FCSTD DOCUMENT  (FreeCAD 0.19R24276 (Git))
Label: Bearing_fix_22x8x7_P2
License: All rights reserved
LicenseURL: http://en.wikipedia.org/wiki/All_rights_reserved
objects: Sketcher::SketchObject×1, PartDesign::Body×1
note: 2 computed .brp shape members not serialized (recipe doc carries the construction recipe); baked Part::Feature solids carry a one-line shape summary decoded from their .brp

FEATURE [Sketcher::SketchObject] Sketch
  FullyConstrained = true
  MapMode = 5
  Support = -> [XY_Plane]
  sketch-geometry (30):
    g0: Circle CenterX=8.3 CenterY=-44.5 CenterZ=0 NormalX=0 NormalY=0 NormalZ=1 AngleXU=0 Radius=2.5
    g1: Circle CenterX=26.7 CenterY=-44.5 CenterZ=0 NormalX=0 NormalY=0 NormalZ=1 AngleXU=0 Radius=2.5
    g2: Circle CenterX=8.3 CenterY=-23.5 CenterZ=0 NormalX=0 NormalY=0 NormalZ=1 AngleXU=0 Radius=2.5
    g3: Circle CenterX=26.7 CenterY=-23.5 CenterZ=0 NormalX=0 NormalY=0 NormalZ=1 AngleXU=0 Radius=2.5
    g4: LineSegment StartX=0 StartY=-50 StartZ=0 EndX=35 EndY=-50 EndZ=0
    g5: LineSegment StartX=35 StartY=-50 StartZ=0 EndX=35 EndY=0 EndZ=0
    g6: LineSegment StartX=35 StartY=0 StartZ=0 EndX=0 EndY=0 EndZ=0
    g7: LineSegment StartX=0 StartY=0 StartZ=0 EndX=0 EndY=-50 EndZ=0
    g8: LineSegment StartX=8.3 StartY=-44.5 StartZ=0 EndX=26.7 EndY=-23.5 EndZ=0
    g9: LineSegment StartX=8.3 StartY=-23.5 StartZ=0 EndX=26.7 EndY=-44.5 EndZ=0
    g10: GeomPoint X=17.5 Y=-34 Z=0
    g11: GeomPoint X=17.5 Y=-34 Z=0
    g12: Circle CenterX=17.5 CenterY=-34 CenterZ=0 NormalX=0 NormalY=0 NormalZ=1 AngleXU=0 Radius=5.5
    g13: LineSegment StartX=17.5 StartY=-34 StartZ=0 EndX=17.5 EndY=-50 EndZ=0
    g14: Circle CenterX=17.5 CenterY=-34 CenterZ=0 NormalX=0 NormalY=0 NormalZ=1 AngleXU=0 Radius=6
    g15: LineSegment StartX=49 StartY=10 StartZ=0 EndX=106 EndY=10 EndZ=0
    g16: LineSegment StartX=106 StartY=10 StartZ=0 EndX=106 EndY=67 EndZ=0
    g17: LineSegment StartX=106 StartY=67 StartZ=0 EndX=49 EndY=67 EndZ=0
    g18: LineSegment StartX=49 StartY=67 StartZ=0 EndX=49 EndY=10 EndZ=0
    g19: LineSegment StartX=49 StartY=67 StartZ=0 EndX=106 EndY=10 EndZ=0
    g20: LineSegment StartX=49 StartY=10 StartZ=0 EndX=106 EndY=67 EndZ=0
    g21: GeomPoint X=77.5 Y=38.5 Z=0
    g22: GeomPoint X=77.5 Y=38.5 Z=0
    g23: Circle CenterX=77.5 CenterY=38.5 CenterZ=0 NormalX=0 NormalY=0 NormalZ=1 AngleXU=0 Radius=6
    g24: LineSegment StartX=12.8776 StartY=-30.1746 StartZ=0 EndX=72.8776 EndY=42.3254 EndZ=0
    g25: LineSegment StartX=82.1224 StartY=34.6746 StartZ=0 EndX=22.1224 EndY=-37.8254 EndZ=0
    g26: LineSegment StartX=72.8776 StartY=42.3254 StartZ=0 EndX=77.5 EndY=38.5 EndZ=0
    g27: LineSegment StartX=77.5 StartY=38.5 StartZ=0 EndX=82.1224 EndY=34.6746 EndZ=0
    g28: LineSegment StartX=12.8776 StartY=-30.1746 StartZ=0 EndX=17.5 EndY=-34 EndZ=0
    g29: LineSegment StartX=17.5 StartY=-34 StartZ=0 EndX=22.1224 EndY=-37.8254 EndZ=0
  constraints (73):
    c: Diameter(g0) = 5
    c: Equal(g0,g1)
    c: Equal(g0,g3)
    c: Equal(g0,g2)
    c: Coincident(g4,g5)
    c: Coincident(g5,g6)
    c: Coincident(g6,g7)
    c: Coincident(g7,g4)
    c: Coincident(g8,g0)
    c: Coincident(g8,g3)
    c: Coincident(g9,g2)
    c: Coincident(g9,g1)
    c: PointOnObject(g10,g8)
    c: PointOnObject(g11,g9)
    c: Coincident(g10,g11)
    c: Coincident(g12,g10)
    c: Diameter(g12) = 11
    c: Coincident(g13,g10)
    c: Symmetric(g4,g4,g13)
    c: Coincident(g14,g10)
    c: Diameter(g14) = 12
    c: DistanceY(g5,g5) = 50
    c: Coincident(g6,g-1)
    c: Vertical(g5)
    c: Vertical(g7)
    c: Vertical(g3,g1)
    c: Vertical(g2,g0)
    c: Horizontal(g4)
    c: DistanceY(g4,g1) = 5.5
    c: Horizontal(g0,g1)
    c: DistanceY(g1,g3) = 21
    c: Horizontal(g6)
    c: DistanceX(g6,g6) = 35
    c: Vertical(g13)
    c: Horizontal(g2,g3)
    c: DistanceX(g2,g3) = 18.4
    c: Coincident(g15,g16)
    c: Coincident(g16,g17)
    c: Coincident(g17,g18)
    c: Coincident(g18,g15)
    c: Horizontal(g15)
    c: Horizontal(g17)
    c: Vertical(g16)
    c: Vertical(g18)
    c: Equal(g15,g16)
    c: DistanceX(g17,g17) = 57
    c: Coincident(g19,g17)
    c: Coincident(g19,g15)
    c: Coincident(g20,g15)
    c: Coincident(g20,g16)
    c: PointOnObject(g21,g19)
    c: PointOnObject(g22,g20)
    c: Coincident(g21,g22)
    c: Coincident(g23,g21)
    c: Diameter(g23) = 12
    c: PointOnObject(g24,g14)
    c: PointOnObject(g24,g23)
    c: Tangent(g24,g23)
    c: PointOnObject(g25,g23)
    c: PointOnObject(g25,g14)
    c: Coincident(g26,g24)
    c: Coincident(g26,g21)
    c: Coincident(g27,g21)
    c: Coincident(g27,g25)
    c: Parallel(g27,g26)
    c: Coincident(g28,g24)
    c: Coincident(g28,g10)
    c: Coincident(g29,g10)
    c: Coincident(g29,g25)
    c: Parallel(g28,g29)
    c: Perpendicular(g24,g28)
    c: DistanceY(g5,g15) = 10
    c: DistanceX(g10,g21) = 60
FEATURE [PartDesign::Body] Body
  Group = -> [Sketch]
  Origin = -> Origin
